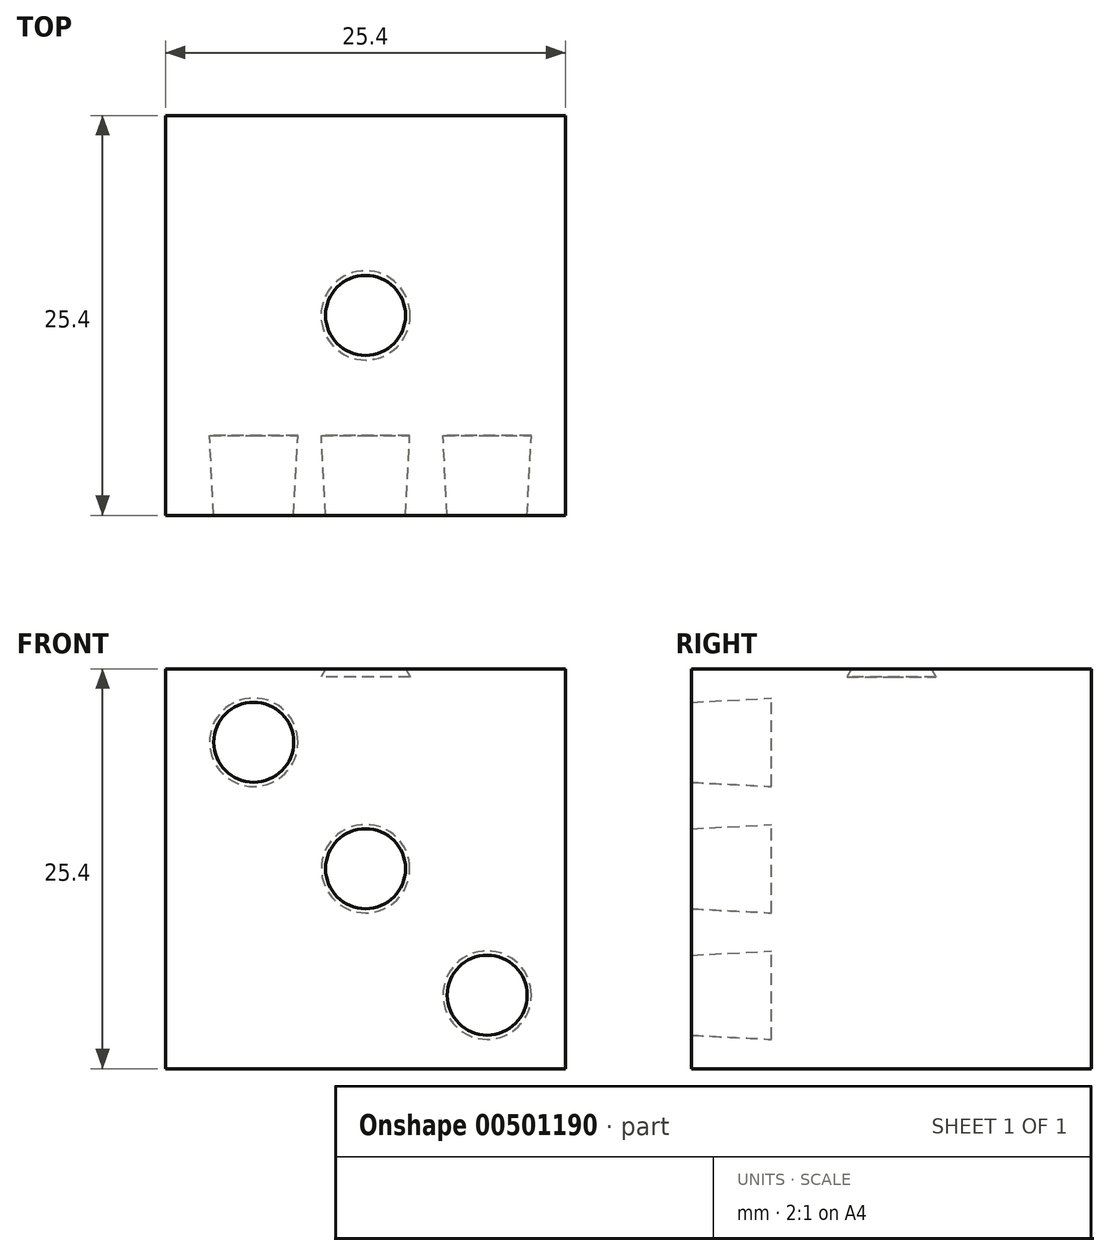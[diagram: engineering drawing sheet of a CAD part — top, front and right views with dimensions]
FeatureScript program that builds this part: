
annotation { "Feature Type Name" : "Feature", "Feature Type Description" : "" }
export const myFeature = defineFeature(function(context is Context, id is Id, definition is map)
    precondition{}
    {
        {
            var Q0;
            Q0=qCreatedBy(makeId("Front.planeOp"),FACE);
            var sketch = newSketch(context, id + "F0", { "sketchPlane" : qUnion([Q0])});
            skLineSegment(sketch, "E0.bottom", {"start": v(12.7, -12.7) * mm, "end": v(-12.7, -12.7) * mm});
            skLineSegment(sketch, "E0.top", {"start": v(12.7, 12.7) * mm, "end": v(-12.7, 12.7) * mm});
            skLineSegment(sketch, "E0.left", {"start": v(12.7, -12.7) * mm, "end": v(12.7, 12.7) * mm});
            skLineSegment(sketch, "E0.right", {"start": v(-12.7, -12.7) * mm, "end": v(-12.7, 12.7) * mm});
            skPoint(sketch, "E0.middle", {"position": v(0, 0) * mm});
            skSolve(sketch);
        }
        {
            var Q0;
            Q0=makeQuery(id+"F0.imprint","IMPRINT",FACE,{"disambiguationData":[TD([[makeQuery(id+"F0.imprint","IMPRINT",EDGE,{"derivedFrom":sQuery(id+"F0.wireOp",EDGE,"E0.bottom")}),-1.0]])]});
            extrude(context, id + "F1", {"entities" : qUnion([Q0]), "depth" : 25.4 * mm});
        }
        {
            var Q0;
            Q0=makeQuery(id+"F1.opExtrude","SWEPT_FACE",FACE,{"disambiguationData":[OSD([sQuery(id+"F0.wireOp",EDGE,"E0.top")])]});
            var sketch = newSketch(context, id + "F2", { "sketchPlane" : qUnion([Q0])});
            skCircle(sketch, "E1", {"center": v(0, -12.7) * mm, "radius": 2.54 * mm});
            skPoint(sketch, "E1.centerSnap0", {"position": v(-12.7, -12.7) * mm});
            skSolve(sketch);
        }
        {
            var Q0;
            Q0=makeQuery(id+"F2.imprint","IMPRINT",FACE,{"disambiguationData":[TD([[makeQuery(id+"F2.imprint","IMPRINT",EDGE,{"derivedFrom":sQuery(id+"F2.wireOp",EDGE,"E1")}),1.0]])]});
            extrude(context, id + "F3", {"entities" : qUnion([Q0]), "operationType" : NewBodyOperationType.REMOVE, "oppositeDirection" : true, "depth" : 0.5 * mm, "hasDraft" : true, "draftAngle" : 30 * degree});
        }
        {
            var Q0;
            Q0=makeQuery(id+"F1.opExtrude","CAP_FACE",FACE,{"disambiguationData":[OSD([sQuery(id+"F0.wireOp",EDGE,"E0.bottom"),sQuery(id+"F0.wireOp",EDGE,"E0.top"),sQuery(id+"F0.wireOp",EDGE,"E0.left"),sQuery(id+"F0.wireOp",EDGE,"E0.right")])],"isStart":false});
            var sketch = newSketch(context, id + "F4", { "sketchPlane" : qUnion([Q0])});
            skCircle(sketch, "E2", {"center": v(0, 0) * mm, "radius": 2.54 * mm});
            skCircle(sketch, "E3", {"center": v(-7.1, 8.03) * mm, "radius": 2.54 * mm});
            skCircle(sketch, "E4", {"center": v(7.72, -8.03) * mm, "radius": 2.54 * mm});
            skSolve(sketch);
        }
        {
            var Q0;
            Q0 = qSketchRegion(id + "F4", true);
            extrude(context, id + "F5", {"entities" : qUnion([Q0]), "operationType" : NewBodyOperationType.REMOVE, "oppositeDirection" : true, "depth" : 5.08 * mm, "hasDraft" : true, "draftAngle" : 3 * degree});
        }
        {
            var Q0;
            Q0=makeQuery(id+"F1.opExtrude","SWEPT_FACE",FACE,{"disambiguationData":[OSD([sQuery(id+"F0.wireOp",EDGE,"E0.left")])]});
            var sketch = newSketch(context, id + "F6", { "sketchPlane" : qUnion([Q0])});
            skCircle(sketch, "E5", {"center": v(-21.62, 8.96) * mm, "radius": 2.54 * mm});
            skCircle(sketch, "E6", {"center": v(-21.62, 0.05) * mm, "radius": 2.54 * mm});
            skCircle(sketch, "E7", {"center": v(-21.62, -8.5) * mm, "radius": 2.54 * mm});
            skCircle(sketch, "E8", {"center": v(-4.52, 8.96) * mm, "radius": 2.54 * mm});
            skCircle(sketch, "E9", {"center": v(-4.52, 0.05) * mm, "radius": 2.54 * mm});
            skCircle(sketch, "E10", {"center": v(-4.52, -8.5) * mm, "radius": 2.54 * mm});
            skSolve(sketch);
        }
        {
            var Q0;
            Q0=sQuery(id+"F6.wireOp",EDGE,"E7");
            var Q1;
            Q1=sQuery(id+"F6.wireOp",EDGE,"E6");
            var Q2;
            Q2=sQuery(id+"F6.wireOp",EDGE,"E5");
            var Q3;
            Q3=sQuery(id+"F6.wireOp",EDGE,"E8");
            var Q4;
            Q4=sQuery(id+"F6.wireOp",EDGE,"E9");
            var Q5;
            Q5=sQuery(id+"F6.wireOp",EDGE,"E10");
            extrude(context, id + "F7", {"bodyType" : ToolBodyType.SURFACE, "surfaceEntities" : qUnion([Q0, Q1, Q2, Q3, Q4, Q5]), "oppositeDirection" : true, "depth" : 5.08 * mm});
        }
    });
